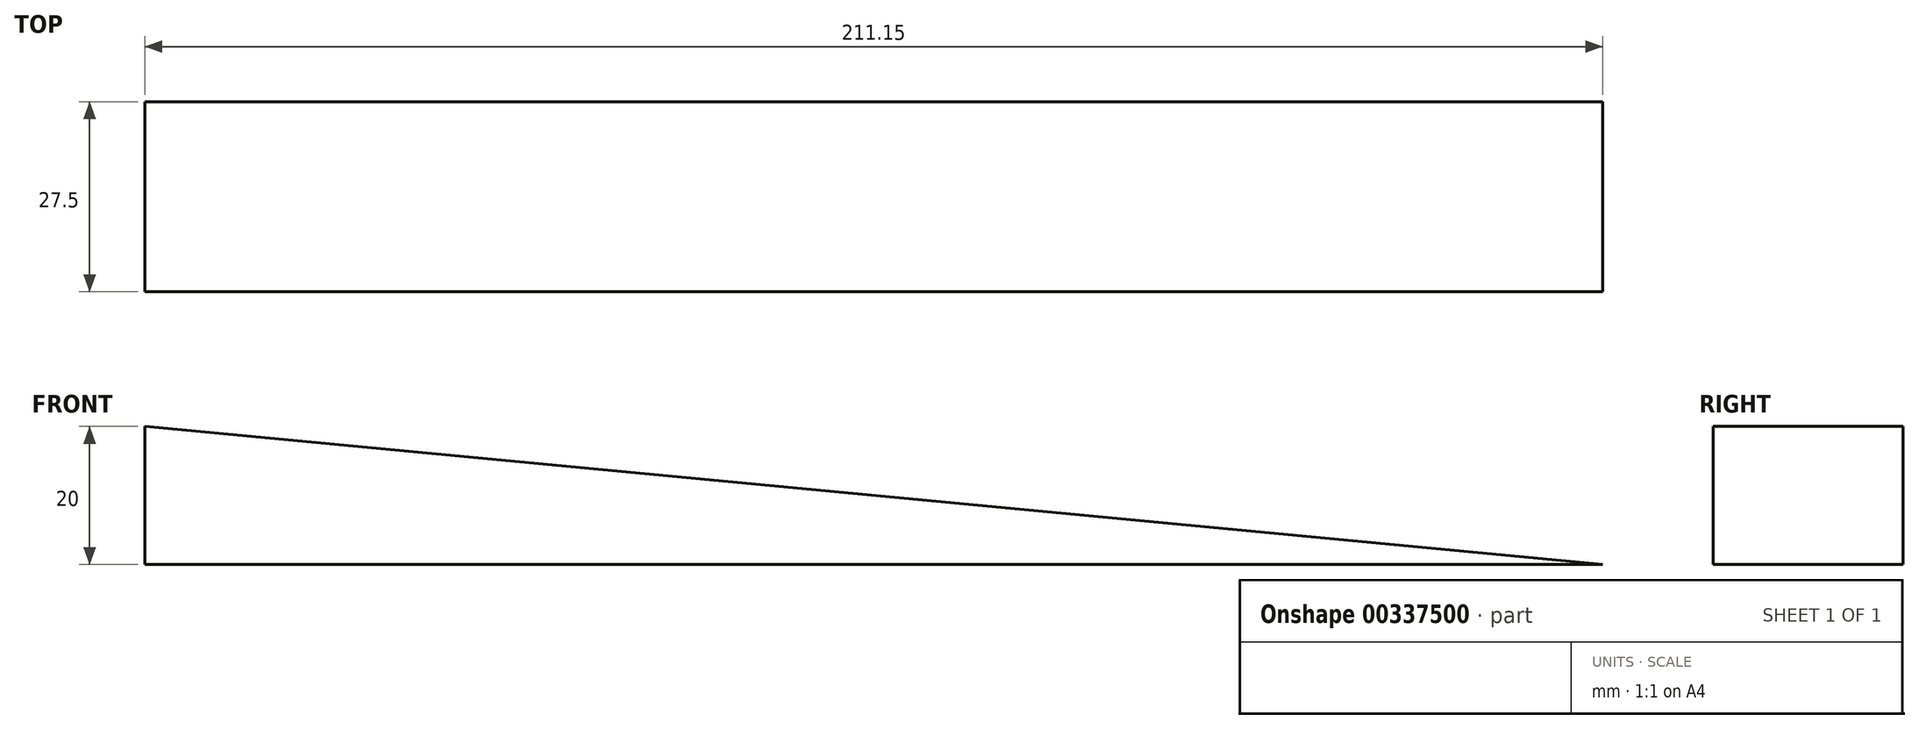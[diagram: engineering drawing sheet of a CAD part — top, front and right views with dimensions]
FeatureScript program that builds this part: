
annotation { "Feature Type Name" : "Feature", "Feature Type Description" : "" }
export const myFeature = defineFeature(function(context is Context, id is Id, definition is map)
    precondition{}
    {
        {
            var Q0;
            Q0=qCreatedBy(makeId("Front.planeOp"),FACE);
            var sketch = newSketch(context, id + "F0", { "sketchPlane" : qUnion([Q0])});
            skLineSegment(sketch, "E0.top", {"start": v(-105.97, -10.4) * mm, "end": v(105.18, -10.4) * mm});
            skLineSegment(sketch, "E0.left", {"start": v(-105.97, 9.6) * mm, "end": v(-105.97, -10.4) * mm});
            skLineSegment(sketch, "E1", {"start": v(-105.97, 9.6) * mm, "end": v(105.18, -10.4) * mm});
            skSolve(sketch);
        }
        {
            var Q0;
            Q0 = qSketchRegion(id + "F0", true);
            extrude(context, id + "F1", {"entities" : qUnion([Q0]), "depth" : 27.5 * mm});
        }
    });
